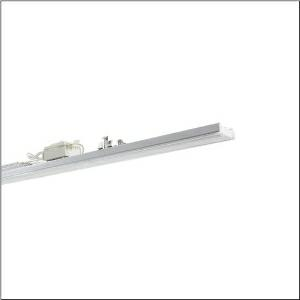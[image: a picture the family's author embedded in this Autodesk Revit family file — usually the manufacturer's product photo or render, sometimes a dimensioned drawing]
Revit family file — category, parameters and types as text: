
# Revit family: licross_r__21_recessed_ho_52te11dv4l2s_a4a6
name_source: partatom
category: Lighting Fixtures
units: mm (PartAtom-declared; Revit-internal decimal feet)

## family parameters
Cut with Voids When Loaded = No
Host = Face
Light Source = No
Part Type = Normal
Room Calculation Point = No
Round Connector Dimension = Use Diameter
Shared = No

## types (1)
- --- (1 x LED, 22660 lm, 125.6 W, 4000K)
    Apparent Load = 126 VA
    CIE Flux Codes = 87 95 99 100 100
    Color Rendering = 80
    Color Temperature = 4000K
    Default Elevation = 1800 mm
    Description = Licross® 21 Recessed HO, luminaire insert, of sheet steel, galvanised, coil coated, white, length: 2.250mm, width: 66mm, height: 67mm, LED rated luminous flux: 22.660lm, light colour: 840, control gear: DALI 2, with plug, 5-pole, with phase selection, mains connection: 220..240V, AC, 50/60Hz, rated input power: 126W, halogen-free wiring, primary light control with lens, of plastic, primary optical cover: cover, of PMMA, light emission: direct distribution, primary light characteristic: symmetric, protection rating (complete): IP54, insulation class (complete): insulation class I (protective earthing), certification: CE, ENEC, VDE, UKCA, protection symbol: D if used in an environment with non-conductive dust loads with corresponding accessories, impact resistance: IK06, permissible ambient temperature for indoor applications: -40..+30°C, corresponds to IFS (International Featured Standards) requirements for safety and quality in the food industry, reducing of maximum allowable ambient temperature of 5°C with ceiling mounting, LABS conformity tested according to VDMA 24364:2018-05, packaging unit: 1 piece
    Height = 58 mm
    Lamp = 1 x LED
    Lamp Light Flux = 22660 lm
    Lamp Power = 125.6 W
    Lamp count = 1
    Length = 2250 mm
    Luminous efficacy = 180 lm/W
    Manufacturer = Siteco
    ModVariant = No
    Model = 52TE11DV4L2S
    Mounting Place = Ceiling
    Mounting Type = Pendant
    Number of Poles = 1
    OnlyDefault = Yes
    Power Factor = 1
    Product Name = Licross® 21 Recessed HO
    Product group = luminaire insert
    ProductGroupID = 902
    Protection Class = Protection class I
    Protection Degree = IP 54
    RLX_Detail_Level = 1
    RLX_Emergency_Light_Flux = 0 lm
    RLX_Emergency_Type = 0
    RLX_Emergency_Type_DB = No
    RlxData = <blob elided: 29629 chars, md5=936b16dd>
    Socket = socket
    Standby Power = 0 W
    System Light Flux = 22659 lm
    System Power = 126 W
    Type Comments = factory setting: luminous flux: 100 % | dim-lin: 254 | 489 mA
    Type Image = l_1296930.jpg
    URL = http://relux.com
    VarID = @adj_127378
    Voltage = 0 V
    Weight = 0.00 kg
    Width = 66 mm

## geometry (parser evidence)
native form markers: Blend x4, Sweep x8
no freeform markers — native parametric forms only
